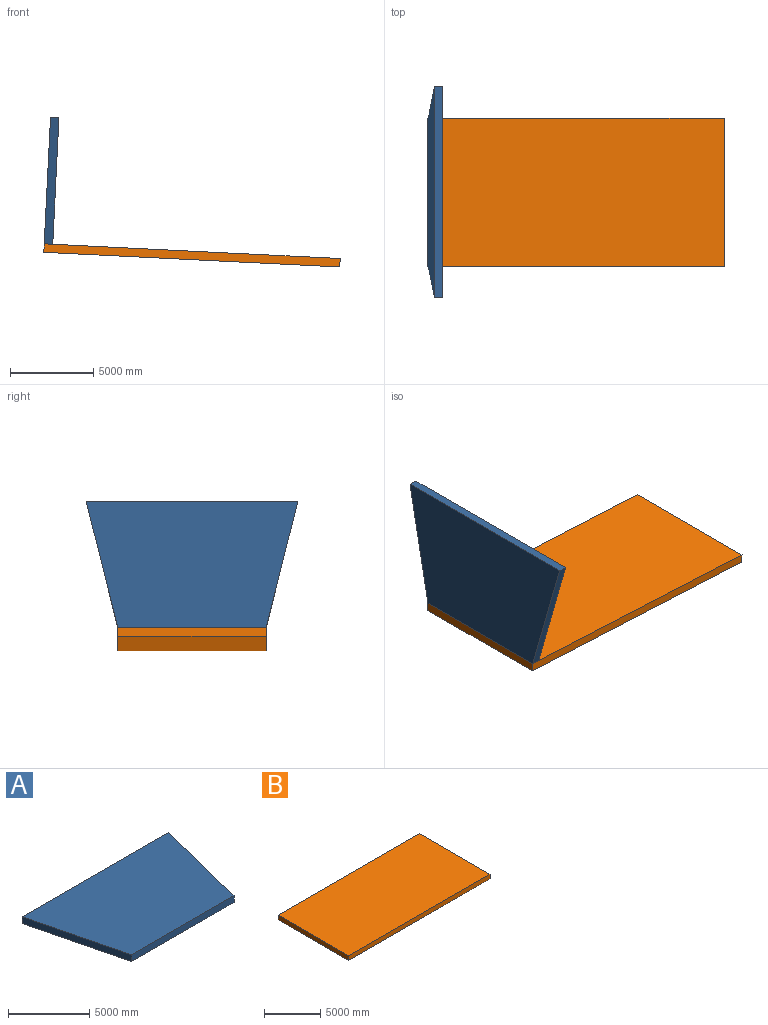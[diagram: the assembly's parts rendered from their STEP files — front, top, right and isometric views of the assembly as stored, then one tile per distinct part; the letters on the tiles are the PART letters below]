
ASSEMBLY  parts=2 mates=1
PART A: 6 faces, bbox 12700x7620x508 mm
  f0: plane 12700x508mm, normal (0,1,0), area 6451600mm2, adj f1,f3,f4,f5
  f1: plane 7620x1905mm, normal (-0.97,-0.24,0), area 3990094.2mm2, adj f0,f2,f4,f5
  f2: plane 8890x508mm, normal (0,-1,0), area 4516120mm2, adj f1,f3,f4,f5
  f3: plane 7620x1905mm, normal (0.97,-0.24,0), area 3990094.2mm2, adj f0,f2,f4,f5
  f4: plane 12700x7620mm, normal (0,0,1), area 82257900mm2, adj f0,f1,f2,f3
  f5: plane 12700x7620mm, normal (0,0,-1), area 82257900mm2, adj f0,f1,f2,f3
PART B: 6 faces, bbox 17780x8890x508 mm
  f0: plane 8890x508mm, normal (1,0,0), area 4516120mm2, adj f1,f3,f4,f5
  f1: plane 17780x508mm, normal (0,1,0), area 9032240mm2, adj f0,f2,f4,f5
  f2: plane 8890x508mm, normal (-1,0,0), area 4516120mm2, adj f1,f3,f4,f5
  f3: plane 17780x508mm, normal (0,-1,0), area 9032240mm2, adj f0,f2,f4,f5
  f4: plane 17780x8890mm, normal (0,0,1), area 158064200mm2, adj f0,f1,f2,f3
  f5: plane 17780x8890mm, normal (0,0,-1), area 158064200mm2, adj f0,f1,f2,f3
PLACE A rot(axis=(0.57,-0.57,-0.6),118.4deg) t=(-23896.81,-3800.94,-18342.33)mm
PLACE B rot(axis=(0,1,0),2.8deg) t=(-15550.29,-3800.94,-19265.16)mm
MATE planar A.f2 <-> B.f4  axis (-0.05,0,-1) through (-24150.5,-3800.94,-18329.74)mm
